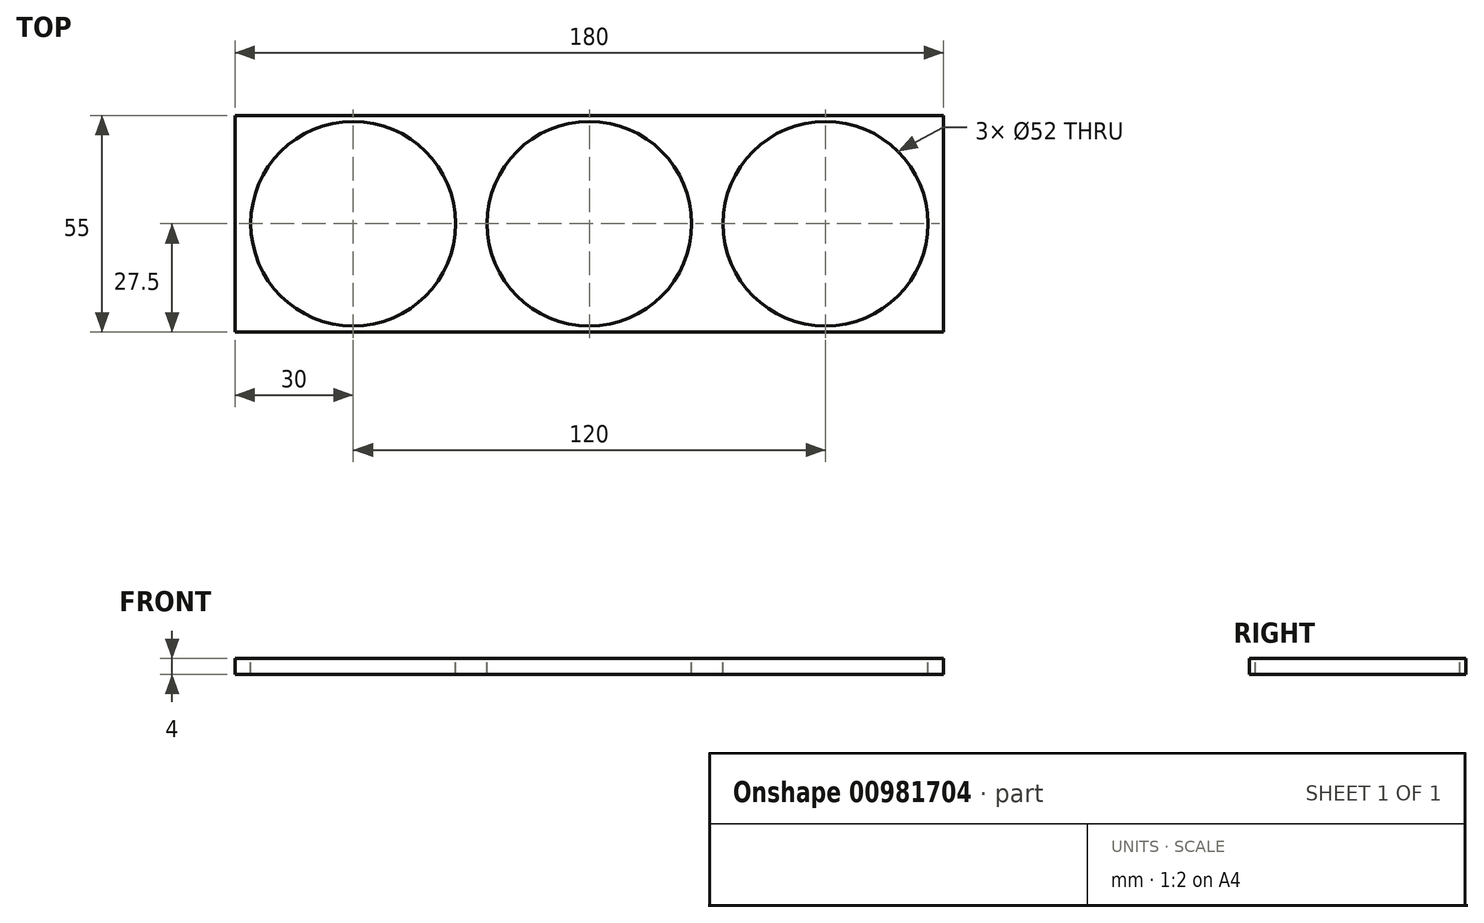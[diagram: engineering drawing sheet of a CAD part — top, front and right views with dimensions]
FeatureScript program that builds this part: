
annotation { "Feature Type Name" : "Feature", "Feature Type Description" : "" }
export const myFeature = defineFeature(function(context is Context, id is Id, definition is map)
    precondition{}
    {
        {
            var Q0;
            Q0=qCreatedBy(makeId("Top.planeOp"),FACE);
            var sketch = newSketch(context, id + "F0", { "sketchPlane" : qUnion([Q0])});
            skLineSegment(sketch, "E0.bottom", {"start": v(0, 0) * mm, "end": v(180, 0) * mm});
            skLineSegment(sketch, "E0.top", {"start": v(0, 55) * mm, "end": v(180, 55) * mm});
            skLineSegment(sketch, "E0.left", {"start": v(0, 0) * mm, "end": v(0, 55) * mm});
            skLineSegment(sketch, "E0.right", {"start": v(180, 0) * mm, "end": v(180, 55) * mm});
            skSolve(sketch);
        }
        {
            var Q0;
            Q0=makeQuery(id+"F0.imprint","IMPRINT",FACE,{"disambiguationData":[TD([[makeQuery(id+"F0.imprint","IMPRINT",EDGE,{"derivedFrom":sQuery(id+"F0.wireOp",EDGE,"E0.bottom")}),1.0]])]});
            extrude(context, id + "F1", {"entities" : qUnion([Q0]), "depth" : (4) * mm, "offsetDistance" : 25 * mm});
        }
        {
            var Q0;
            Q0=makeQuery(id+"F1.opExtrude","CAP_FACE",FACE,{"disambiguationData":[OSD([sQuery(id+"F0.wireOp",EDGE,"E0.bottom"),sQuery(id+"F0.wireOp",EDGE,"E0.top"),sQuery(id+"F0.wireOp",EDGE,"E0.left"),sQuery(id+"F0.wireOp",EDGE,"E0.right")])],"isStart":false});
            var sketch = newSketch(context, id + "F2", { "sketchPlane" : qUnion([Q0])});
            skCircle(sketch, "E1", {"center": v(90, 27.5) * mm, "radius": 26 * mm});
            skCircle(sketch, "E2", {"center": v(30, 27.5) * mm, "radius": 26 * mm});
            skCircle(sketch, "E3", {"center": v(150, 27.5) * mm, "radius": 26 * mm});
            skLineSegment(sketch, "E4", {"start": v(90, 55) * mm, "end": v(90, 0) * mm, "construction": true});
            skLineSegment(sketch, "E5", {"start": v(30, 27.5) * mm, "end": v(90, 27.5) * mm, "construction": true});
            skLineSegment(sketch, "E6", {"start": v(90, 27.5) * mm, "end": v(150, 27.5) * mm, "construction": true});
            skSolve(sketch);
        }
        {
            var Q0;
            Q0=makeQuery(id+"F2.imprint","IMPRINT",FACE,{"disambiguationData":[TD([[makeQuery(id+"F2.imprint","IMPRINT",EDGE,{"derivedFrom":sQuery(id+"F2.wireOp",EDGE,"E2")}),1.0]])]});
            var Q1;
            Q1=makeQuery(id+"F2.imprint","IMPRINT",FACE,{"disambiguationData":[TD([[makeQuery(id+"F2.imprint","IMPRINT",EDGE,{"derivedFrom":sQuery(id+"F2.wireOp",EDGE,"E1")}),1.0]])]});
            var Q2;
            Q2=makeQuery(id+"F2.imprint","IMPRINT",FACE,{"disambiguationData":[TD([[makeQuery(id+"F2.imprint","IMPRINT",EDGE,{"derivedFrom":sQuery(id+"F2.wireOp",EDGE,"E3")}),1.0]])]});
            extrude(context, id + "F3", {"entities" : qUnion([Q0, Q1, Q2]), "operationType" : NewBodyOperationType.REMOVE, "endBound" : BoundingType.THROUGH_ALL, "oppositeDirection" : true, "depth" : 25 * mm, "offsetDistance" : 25 * mm});
        }
    });
